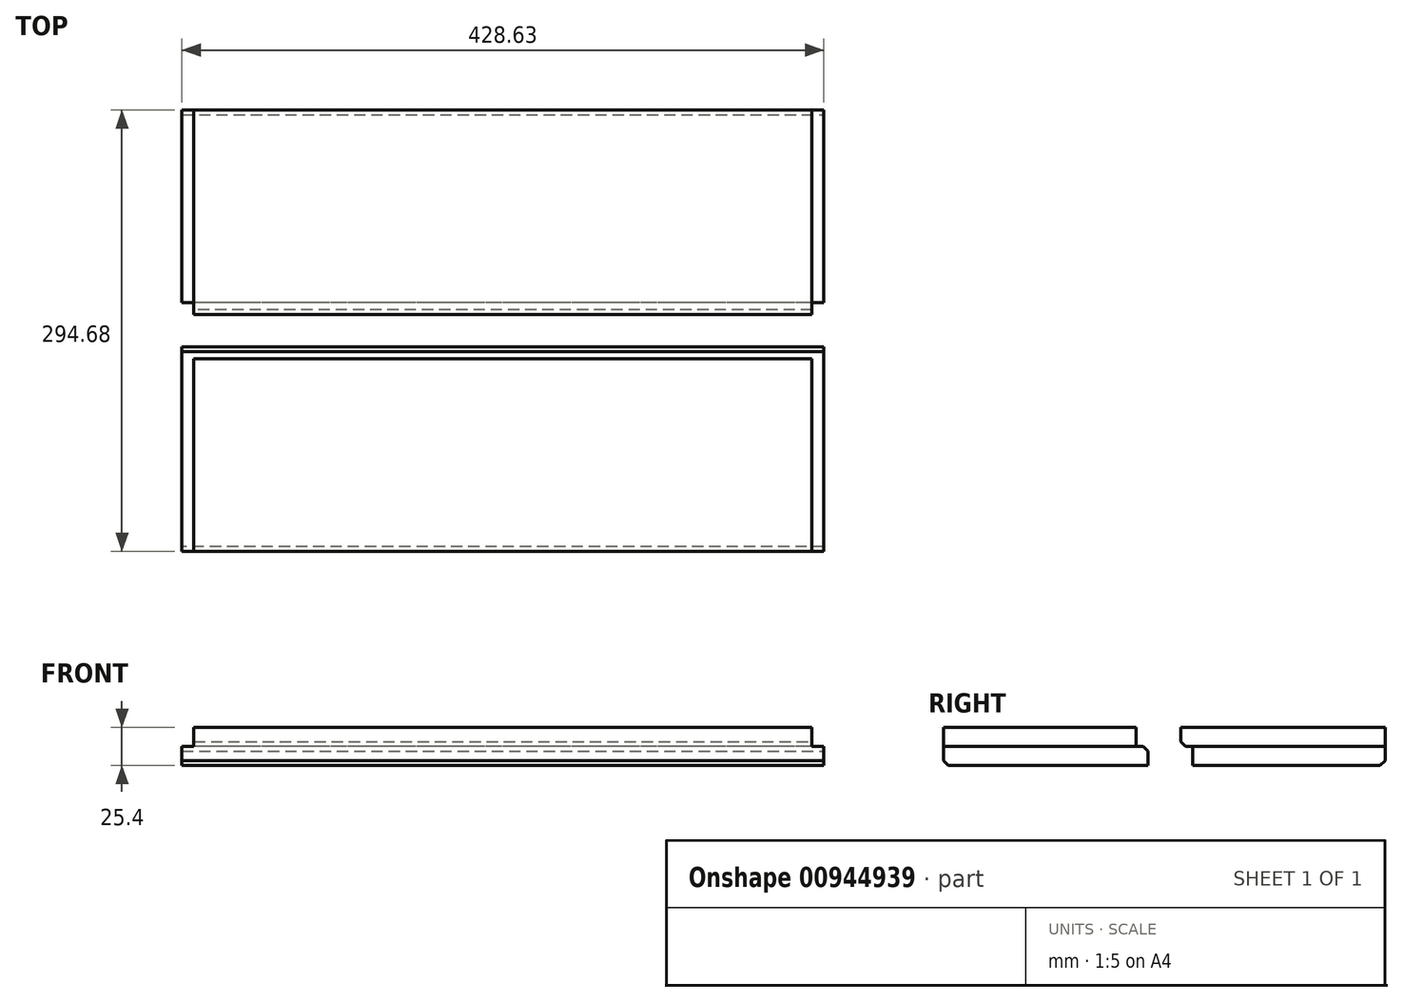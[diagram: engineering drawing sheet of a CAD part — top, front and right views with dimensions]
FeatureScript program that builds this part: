
annotation { "Feature Type Name" : "Feature", "Feature Type Description" : "" }
export const myFeature = defineFeature(function(context is Context, id is Id, definition is map)
    precondition{}
    {
        {
            var Q0;
            Q0=qCreatedBy(makeId("Right.planeOp"),FACE);
            var sketch = newSketch(context, id + "F0", { "sketchPlane" : qUnion([Q0])});
            skLineSegment(sketch, "E0.bottom", {"start": v(-174.97, -9.2) * mm, "end": v(-46.39, -9.2) * mm});
            skLineSegment(sketch, "E0.top", {"start": v(-174.97, -34.6) * mm, "end": v(-46.39, -34.6) * mm});
            skLineSegment(sketch, "E0.left", {"start": v(-174.97, -9.2) * mm, "end": v(-174.97, -34.6) * mm});
            skLineSegment(sketch, "E0.right", {"start": v(-46.39, -9.2) * mm, "end": v(-46.39, -34.6) * mm});
            skPoint(sketch, "E1.oppositeSnap0", {"position": v(-46.39, -21.9) * mm});
            skLineSegment(sketch, "E1.bottom", {"start": v(-46.39, -34.6) * mm, "end": v(-38.44, -34.6) * mm});
            skLineSegment(sketch, "E1.top", {"start": v(-46.39, -21.9) * mm, "end": v(-38.44, -21.9) * mm});
            skLineSegment(sketch, "E1.left", {"start": v(-46.39, -34.6) * mm, "end": v(-46.39, -21.9) * mm});
            skLineSegment(sketch, "E1.right", {"start": v(-38.44, -34.6) * mm, "end": v(-38.44, -21.9) * mm});
            skLineSegment(sketch, "E2.bottom", {"start": v(-46.39, -21.9) * mm, "end": v(-174.97, -21.9) * mm});
            skLineSegment(sketch, "E2.top", {"start": v(-46.39, -34.6) * mm, "end": v(-174.97, -34.6) * mm});
            skLineSegment(sketch, "E2.left", {"start": v(-46.39, -21.9) * mm, "end": v(-46.39, -34.6) * mm});
            skLineSegment(sketch, "E2.right", {"start": v(-174.97, -21.9) * mm, "end": v(-174.97, -34.6) * mm});
            skLineSegment(sketch, "E3.bottom", {"start": v(-8.88, -9.2) * mm, "end": v(119.71, -9.2) * mm});
            skLineSegment(sketch, "E3.top", {"start": v(-8.88, -34.6) * mm, "end": v(119.71, -34.6) * mm});
            skLineSegment(sketch, "E3.left", {"start": v(-8.88, -9.2) * mm, "end": v(-8.88, -34.6) * mm});
            skLineSegment(sketch, "E3.right", {"start": v(119.71, -9.2) * mm, "end": v(119.71, -34.6) * mm});
            skLineSegment(sketch, "E4.top", {"start": v(-8.88, -21.9) * mm, "end": v(119.71, -21.9) * mm});
            skLineSegment(sketch, "E4.left", {"start": v(-8.88, -34.6) * mm, "end": v(-8.88, -21.9) * mm});
            skLineSegment(sketch, "E4.right", {"start": v(119.71, -34.6) * mm, "end": v(119.71, -21.9) * mm});
            skLineSegment(sketch, "E5.bottom", {"start": v(-8.88, -9.2) * mm, "end": v(-16.81, -9.2) * mm});
            skLineSegment(sketch, "E5.top", {"start": v(-8.88, -21.9) * mm, "end": v(-16.81, -21.9) * mm});
            skLineSegment(sketch, "E5.left", {"start": v(-8.88, -9.2) * mm, "end": v(-8.88, -21.9) * mm});
            skLineSegment(sketch, "E5.right", {"start": v(-16.81, -9.2) * mm, "end": v(-16.81, -21.9) * mm});
            skSolve(sketch);
        }
        {
            var Q0;
            {var subQ0=sQuery(id+"F0.wireOp",EDGE,"E3.bottom");Q0=makeQuery(id+"F0.imprint","IMPRINT",FACE,{"disambiguationData":[TD([[makeQuery(id+"F0.imprint","IMPRINT",EDGE,{"derivedFrom":subQ0}),-1.0]])]});}
            var Q1;
            {var subQ0=sQuery(id+"F0.wireOp",EDGE,"E5.bottom");Q1=makeQuery(id+"F0.imprint","IMPRINT",FACE,{"disambiguationData":[TD([[makeQuery(id+"F0.imprint","IMPRINT",EDGE,{"derivedFrom":subQ0}),1.0]])]});}
            var Q2;
            {var subQ0=sQuery(id+"F0.wireOp",EDGE,"E0.bottom");Q2=makeQuery(id+"F0.imprint","IMPRINT",FACE,{"disambiguationData":[TD([[makeQuery(id+"F0.imprint","IMPRINT",EDGE,{"derivedFrom":subQ0}),-1.0]])]});}
            extrude(context, id + "F1", {"entities" : qUnion([Q0, Q1, Q2]), "depth" : 412.75 * mm, "offsetDistance" : 25.4 * mm});
        }
        {
            var Q0;
            {var subQ0=sQuery(id+"F0.wireOp",EDGE,"E3.top");Q0=makeQuery(id+"F0.imprint","IMPRINT",FACE,{"disambiguationData":[TD([[makeQuery(id+"F0.imprint","IMPRINT",EDGE,{"derivedFrom":subQ0}),1.0]])]});}
            extrude(context, id + "F2", {"entities" : qUnion([Q0]), "operationType" : NewBodyOperationType.ADD, "depth" : 420.7 * mm, "offsetDistance" : 25.4 * mm, "hasSecondDirection" : true, "secondDirectionOppositeDirection" : true, "secondDirectionDepth" : 7.94 * mm});
        }
        {
            var Q0;
            {var subQ0=sQuery(id+"F0.wireOp",EDGE,"E0.top");Q0=makeQuery(id+"F0.imprint","IMPRINT",FACE,{"disambiguationData":[TD([[makeQuery(id+"F0.imprint","IMPRINT",EDGE,{"derivedFrom":subQ0}),1.0]])]});}
            var Q1;
            {var subQ0=sQuery(id+"F0.wireOp",EDGE,"E1.bottom");Q1=makeQuery(id+"F0.imprint","IMPRINT",FACE,{"disambiguationData":[TD([[makeQuery(id+"F0.imprint","IMPRINT",EDGE,{"derivedFrom":subQ0}),1.0]])]});}
            extrude(context, id + "F3", {"entities" : qUnion([Q0, Q1]), "operationType" : NewBodyOperationType.ADD, "depth" : 420.7 * mm, "offsetDistance" : 25.4 * mm, "hasSecondDirection" : true, "secondDirectionOppositeDirection" : true, "secondDirectionDepth" : 7.94 * mm});
        }
        {
            var Q0;
            Q0=makeQuery(id+"F3.opExtrude","SWEPT_EDGE",EDGE,{"disambiguationData":[OSD([sQuery(id+"F0.wireOp",EDGE,"E1.top"),sQuery(id+"F0.wireOp",EDGE,"E1.right")])]});
            var Q1;
            Q1=makeQuery(id+"F1.opExtrude","SWEPT_EDGE",EDGE,{"disambiguationData":[OSD([sQuery(id+"F0.wireOp",EDGE,"E5.top"),sQuery(id+"F0.wireOp",EDGE,"E5.right")])]});
            var Q2;
            Q2=makeQuery(id+"F2.opExtrude","SWEPT_EDGE",EDGE,{"disambiguationData":[OSD([sQuery(id+"F0.wireOp",EDGE,"E3.top"),sQuery(id+"F0.wireOp",EDGE,"E3.right")])]});
            var Q3;
            Q3=makeQuery(id+"F3.opExtrude","SWEPT_EDGE",EDGE,{"disambiguationData":[OSD([sQuery(id+"F0.wireOp",EDGE,"E0.top"),sQuery(id+"F0.wireOp",EDGE,"E0.left")])]});
            chamfer(context, id + "F4", {"entities" : qUnion([Q0, Q1, Q2, Q3]), "width" : 3.17 * mm, "tangentPropagation" : true});
        }
    });
